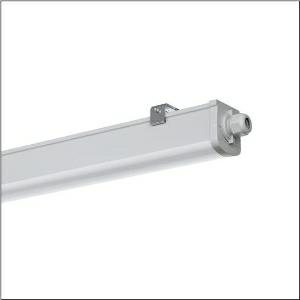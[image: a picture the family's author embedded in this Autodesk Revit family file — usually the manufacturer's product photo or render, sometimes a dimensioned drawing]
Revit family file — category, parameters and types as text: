
# Revit family: monsun_r__31_51fa20dk430b_aae0
name_source: partatom
category: Lighting Fixtures
units: mm (PartAtom-declared; Revit-internal decimal feet)

## family parameters
Cut with Voids When Loaded = No
Host = Face
Light Source = No
Part Type = Normal
Room Calculation Point = No
Round Connector Dimension = Use Diameter
Shared = No

## types (1)
- Monsun® 31 (1 x LED, 3000 lm, 22 W, 4000K)
    Apparent Load = 22 VA
    CIE Flux Codes = 42 72 91 92 100
    Color Rendering = 80
    Color Temperature = 4000K
    Default Elevation = 1800 mm
    Description = Monsun® 31, damp-proof luminaire, primary optical cover: diffuser, of PC, frosted, light emission: direct distribution, primary light characteristic: symmetric, installation type: surface-mounted, LED, rated luminous flux: 3.000lm, luminous efficacy: 136lm/W, light colour: 840, colour temperature: 4000K, control gear: DALI 2, with terminal, 5+1-pole, max. 2.5mm², through-wiring: 3x 2.5mm² + 3x 1.5mm², mains connection: 220..240V, AC, 50/60Hz, rated input power: 22W, housing, luminaire housing, of PC, light grey (RAL 7035), length: 1.158mm, width: 68mm, height: 76mm, protection rating (complete): IP66, insulation class (complete): insulation class II (safety insulation), certification: CE, ENEC, UKCA, protection symbol: D, impact resistance: IK08, permissible operating ambient temperature: -20..+40°C, corresponds to IFS (International Featured Standards) requirements for safety and quality in the food industry, contact your sales advisor before using the luminaires in applications with unclear chemical exposure, large temperature fluctuations or condensation-forming humidity, packaging unit: 1 piece
    Height = 77 mm
    Lamp = 1 x LED
    Lamp Light Flux = 3000 lm
    Lamp Power = 22 W
    Lamp count = 1
    Length = 1218 mm
    Luminous efficacy = 136 lm/W
    Manufacturer = Siteco
    ModVariant = No
    Model = 51FA20DK430B
    Mounting Place = Ceiling
    Mounting Type = Surface mounted
    Number of Poles = 1
    OnlyDefault = Yes
    Power Factor = 1
    Product Name = Monsun® 31
    Product group = damp-proof luminaire
    ProductGroupID = 300
    Protection Class = Protection class II
    Protection Degree = IP 66
    RLX_Detail_Level = 1
    RLX_Emergency_Light_Flux = 0 lm
    RLX_Emergency_Type = 0
    RLX_Emergency_Type_DB = No
    RlxData = <blob elided: 32997 chars, md5=a49f738a>
    Socket = socket
    Standby Power = 0 W
    System Light Flux = 3000 lm
    System Power = 22 W
    Type Comments = Product without accessories
    Type Image = l_1006174.jpg
    URL = http://relux.com
    VarID = ---
    Voltage = 0 V
    Weight = 0.00 kg
    Width = 69 mm

## geometry (parser evidence)
native form markers: Blend x4, Sweep x10
no freeform markers — native parametric forms only
